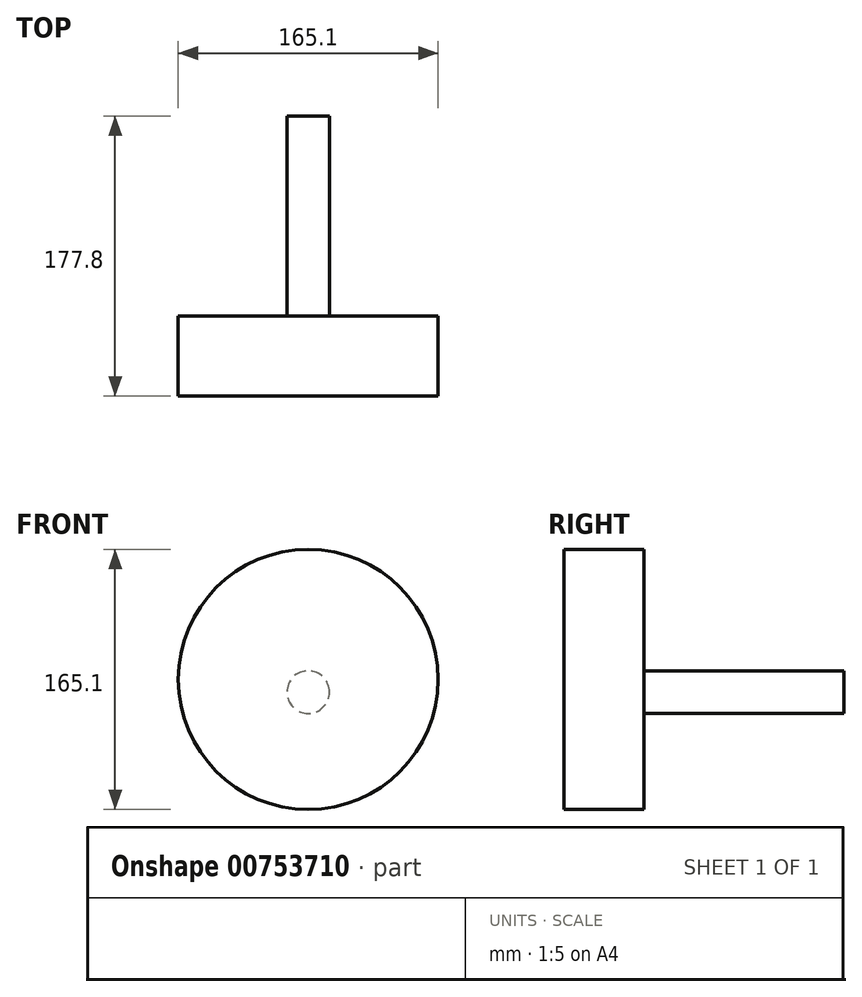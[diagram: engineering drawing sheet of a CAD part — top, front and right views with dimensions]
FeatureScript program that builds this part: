
annotation { "Feature Type Name" : "Feature", "Feature Type Description" : "" }
export const myFeature = defineFeature(function(context is Context, id is Id, definition is map)
    precondition{}
    {
        {
            var Q0;
            Q0=qCreatedBy(makeId("Front.planeOp"),FACE);
            var sketch = newSketch(context, id + "F0", { "sketchPlane" : qUnion([Q0])});
            skCircle(sketch, "E0", {"center": v(0, 0) * mm, "radius": 82.55 * mm});
            skSolve(sketch);
        }
        {
            var Q0;
            Q0=makeQuery(id+"F0.imprint","IMPRINT",FACE,{"disambiguationData":[TD([[makeQuery(id+"F0.imprint","IMPRINT",EDGE,{"derivedFrom":sQuery(id+"F0.wireOp",EDGE,"E0")}),1.0]])]});
            extrude(context, id + "F1", {"entities" : qUnion([Q0]), "depth" : 50.8 * mm, "offsetDistance" : 25.4 * mm});
        }
        {
            var Q0;
            Q0=makeQuery(id+"F1.opExtrude","CAP_FACE",FACE,{"disambiguationData":[OSD([sQuery(id+"F0.wireOp",EDGE,"E0")])],"isStart":true});
            var sketch = newSketch(context, id + "F2", { "sketchPlane" : qUnion([Q0])});
            skCircle(sketch, "E1", {"center": v(0, -8.03) * mm, "radius": 13.5 * mm});
            skSolve(sketch);
        }
        {
            var Q0;
            Q0 = qSketchRegion(id + "F2", true);
            extrude(context, id + "F3", {"entities" : qUnion([Q0]), "operationType" : NewBodyOperationType.ADD, "depth" : 127 * mm, "offsetDistance" : 25.4 * mm});
        }
    });
